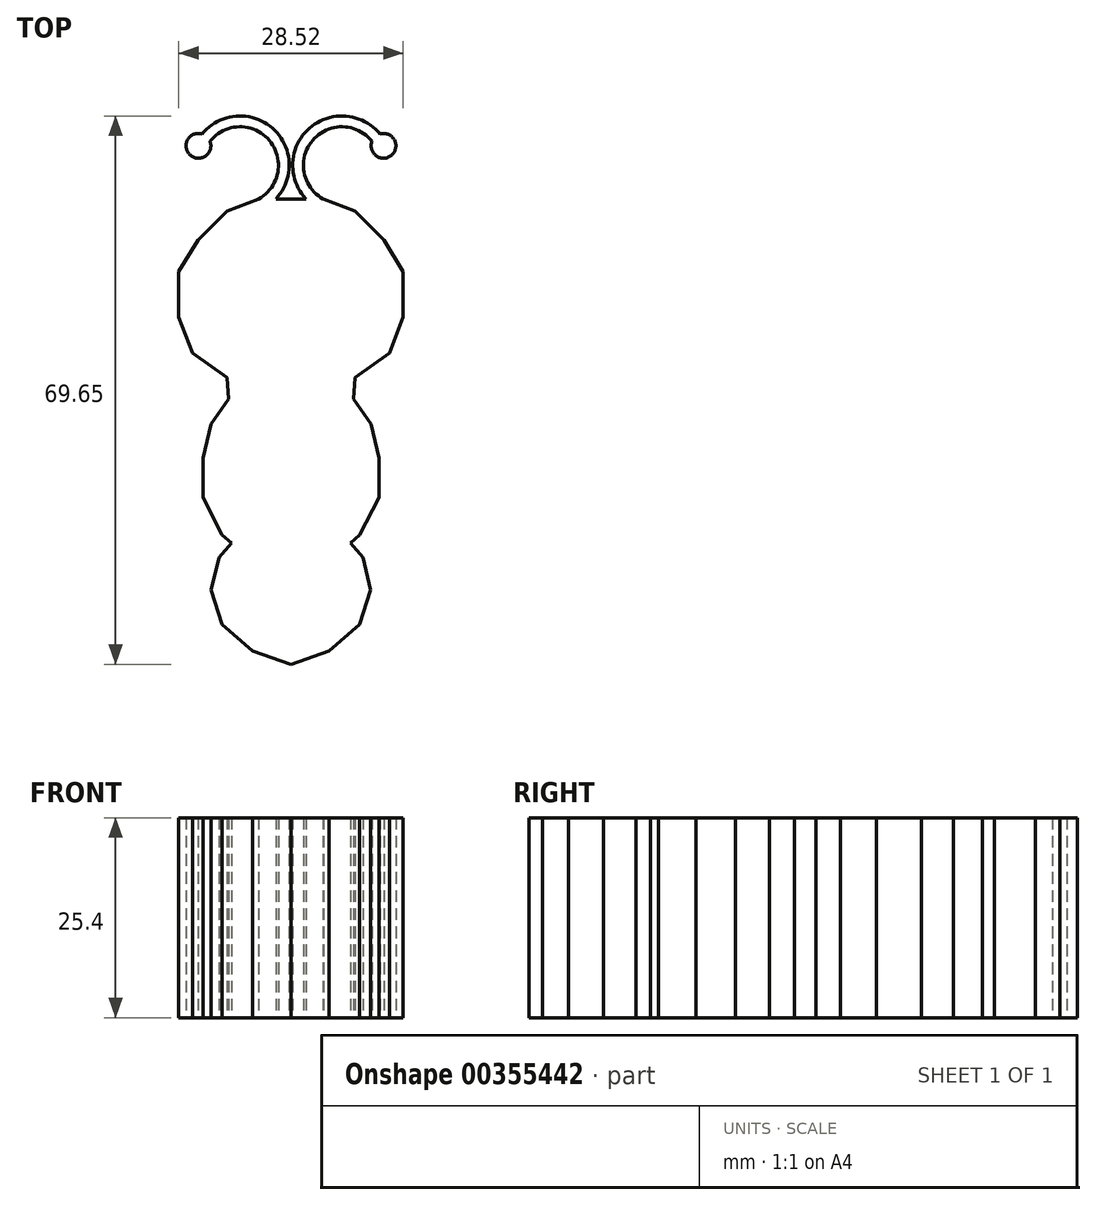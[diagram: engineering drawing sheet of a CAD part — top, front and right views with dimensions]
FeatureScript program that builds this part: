
annotation { "Feature Type Name" : "Feature", "Feature Type Description" : "" }
export const myFeature = defineFeature(function(context is Context, id is Id, definition is map)
    precondition{}
    {
        {
            var Q0;
            Q0=qCreatedBy(makeId("Top.planeOp"),FACE);
            var sketch = newSketch(context, id + "F0", { "sketchPlane" : qUnion([Q0])});
            skLineSegment(sketch, "E0", {"start": v(0, 59.11) * mm, "end": v(1.9, 59.11) * mm});
            skLineSegment(sketch, "E1", {"start": v(4.12, 59.11) * mm, "end": v(8.14, 57.54) * mm});
            skLineSegment(sketch, "E2", {"start": v(8.14, 57.54) * mm, "end": v(11.8, 53.87) * mm});
            skLineSegment(sketch, "E3", {"start": v(11.8, 53.87) * mm, "end": v(14.26, 49.85) * mm});
            skLineSegment(sketch, "E4", {"start": v(14.26, 49.85) * mm, "end": v(14.26, 44.09) * mm});
            skLineSegment(sketch, "E5", {"start": v(14.26, 44.09) * mm, "end": v(12.5, 39.55) * mm});
            skLineSegment(sketch, "E6", {"start": v(12.5, 39.55) * mm, "end": v(8.14, 36.4) * mm});
            skArc(sketch, "E7", {"start": v(11.31, 67.37) * mm, "mid": v(2.35, 68.1) * mm, "end": v(1.9, 59.11) * mm});
            skArc(sketch, "E8", {"start": v(10.3, 66.45) * mm, "mid": v(2.74, 66.55) * mm, "end": v(4.1, 59.11) * mm});
            skCircle(sketch, "E9", {"center": v(11.75, 65.85) * mm, "radius": 1.58 * mm});
            skPoint(sketch, "E10.orphan", {"position": v(11.75, 66.76) * mm});
            skLineSegment(sketch, "E11", {"start": v(7.95, 33.66) * mm, "end": v(10.16, 30.5) * mm});
            skLineSegment(sketch, "E12", {"start": v(10.16, 30.5) * mm, "end": v(11.18, 26.18) * mm});
            skLineSegment(sketch, "E13", {"start": v(11.18, 26.18) * mm, "end": v(11.18, 21.16) * mm});
            skLineSegment(sketch, "E14", {"start": v(11.18, 21.16) * mm, "end": v(8.74, 16.42) * mm});
            skLineSegment(sketch, "E15", {"start": v(8.74, 16.42) * mm, "end": v(7.55, 15.39) * mm});
            skLineSegment(sketch, "E16", {"start": v(7.55, 15.39) * mm, "end": v(9.14, 13.55) * mm});
            skLineSegment(sketch, "E17", {"start": v(9.14, 13.55) * mm, "end": v(10.12, 9.42) * mm});
            skLineSegment(sketch, "E18", {"start": v(10.12, 9.42) * mm, "end": v(8.74, 5.02) * mm});
            skLineSegment(sketch, "E19", {"start": v(8.74, 5.02) * mm, "end": v(4.86, 1.67) * mm});
            skLineSegment(sketch, "E20", {"start": v(4.86, 1.67) * mm, "end": v(0, 0) * mm});
            skPoint(sketch, "E21.orphan", {"position": v(0, 34.48) * mm});
            skPoint(sketch, "E22.end.orphan", {"position": v(0, 12.86) * mm});
            skPoint(sketch, "E22.start.orphan", {"position": v(2.93, 13.55) * mm});
            skPoint(sketch, "E23.orphan", {"position": v(6.36, 14.36) * mm});
            skLineSegment(sketch, "E24.MirrorCS", {"start": v(-12.5, 39.55) * mm, "end": v(-8.14, 36.4) * mm});
            skLineSegment(sketch, "E25.MirrorCS", {"start": v(-8.14, 57.54) * mm, "end": v(-11.8, 53.87) * mm});
            skLineSegment(sketch, "E26.MirrorCS", {"start": v(-11.8, 53.87) * mm, "end": v(-14.26, 49.85) * mm});
            skLineSegment(sketch, "E27.MirrorCS", {"start": v(-7.55, 15.39) * mm, "end": v(-9.14, 13.55) * mm});
            skLineSegment(sketch, "E28.MirrorCS", {"start": v(-4.12, 59.11) * mm, "end": v(-8.14, 57.54) * mm});
            skLineSegment(sketch, "E29.MirrorCS", {"start": v(-8.74, 16.42) * mm, "end": v(-7.55, 15.39) * mm});
            skCircle(sketch, "E30.MirrorC", {"center": v(-11.75, 65.85) * mm, "radius": 1.58 * mm});
            skLineSegment(sketch, "E31.MirrorCS", {"start": v(-7.95, 33.66) * mm, "end": v(-10.16, 30.5) * mm});
            skLineSegment(sketch, "E32.MirrorCS", {"start": v(-11.18, 26.18) * mm, "end": v(-11.18, 21.16) * mm});
            skLineSegment(sketch, "E33.MirrorCS", {"start": v(-8.74, 5.02) * mm, "end": v(-4.86, 1.67) * mm});
            skLineSegment(sketch, "E34.MirrorCS", {"start": v(-11.18, 21.16) * mm, "end": v(-8.74, 16.42) * mm});
            skLineSegment(sketch, "E35.MirrorCS", {"start": v(-14.26, 44.09) * mm, "end": v(-12.5, 39.55) * mm});
            skLineSegment(sketch, "E36.MirrorCS", {"start": v(-10.16, 30.5) * mm, "end": v(-11.18, 26.18) * mm});
            skLineSegment(sketch, "E37.MirrorCS", {"start": v(-10.12, 9.42) * mm, "end": v(-8.74, 5.02) * mm});
            skLineSegment(sketch, "E38.MirrorCS", {"start": v(-9.14, 13.55) * mm, "end": v(-10.12, 9.42) * mm});
            skLineSegment(sketch, "E39.MirrorCS", {"start": v(0, 59.11) * mm, "end": v(-1.9, 59.11) * mm});
            skPoint(sketch, "E40.MirrorP", {"position": v(-11.75, 66.76) * mm});
            skPoint(sketch, "E41.MirrorP", {"position": v(-2.93, 13.55) * mm});
            skArc(sketch, "E42.MirrorCS", {"start": v(-10.3, 66.45) * mm, "mid": v(-2.74, 66.55) * mm, "end": v(-4.1, 59.11) * mm});
            skArc(sketch, "E43.MirrorCS", {"start": v(-11.31, 67.37) * mm, "mid": v(-2.35, 68.1) * mm, "end": v(-1.9, 59.11) * mm});
            skLineSegment(sketch, "E44.MirrorCS", {"start": v(-4.86, 1.67) * mm, "end": v(0, 0) * mm});
            skLineSegment(sketch, "E45.MirrorCS", {"start": v(-14.26, 49.85) * mm, "end": v(-14.26, 44.09) * mm});
            skPoint(sketch, "E46.MirrorP", {"position": v(-6.36, 14.36) * mm});
            skLineSegment(sketch, "E47.trimOffspring", {"start": v(4.1, 59.11) * mm, "end": v(4.12, 59.11) * mm});
            skLineSegment(sketch, "E48.trimOffspring", {"start": v(-4.1, 59.11) * mm, "end": v(-4.12, 59.11) * mm});
            skPoint(sketch, "E49.MirrorCS.start.orphan", {"position": v(-4.07, 35.44) * mm});
            skPoint(sketch, "E50.start.orphan", {"position": v(4.07, 35.44) * mm});
            skLineSegment(sketch, "E51", {"start": v(-8.14, 36.4) * mm, "end": v(-7.95, 33.66) * mm});
            skLineSegment(sketch, "E52", {"start": v(8.14, 36.4) * mm, "end": v(7.95, 33.66) * mm});
            skSolve(sketch);
        }
        {
            var Q0;
            Q0 = qSketchRegion(id + "F0", true);
            extrude(context, id + "F1", {"entities" : qUnion([Q0]), "depth" : 25.4 * mm});
        }
    });
